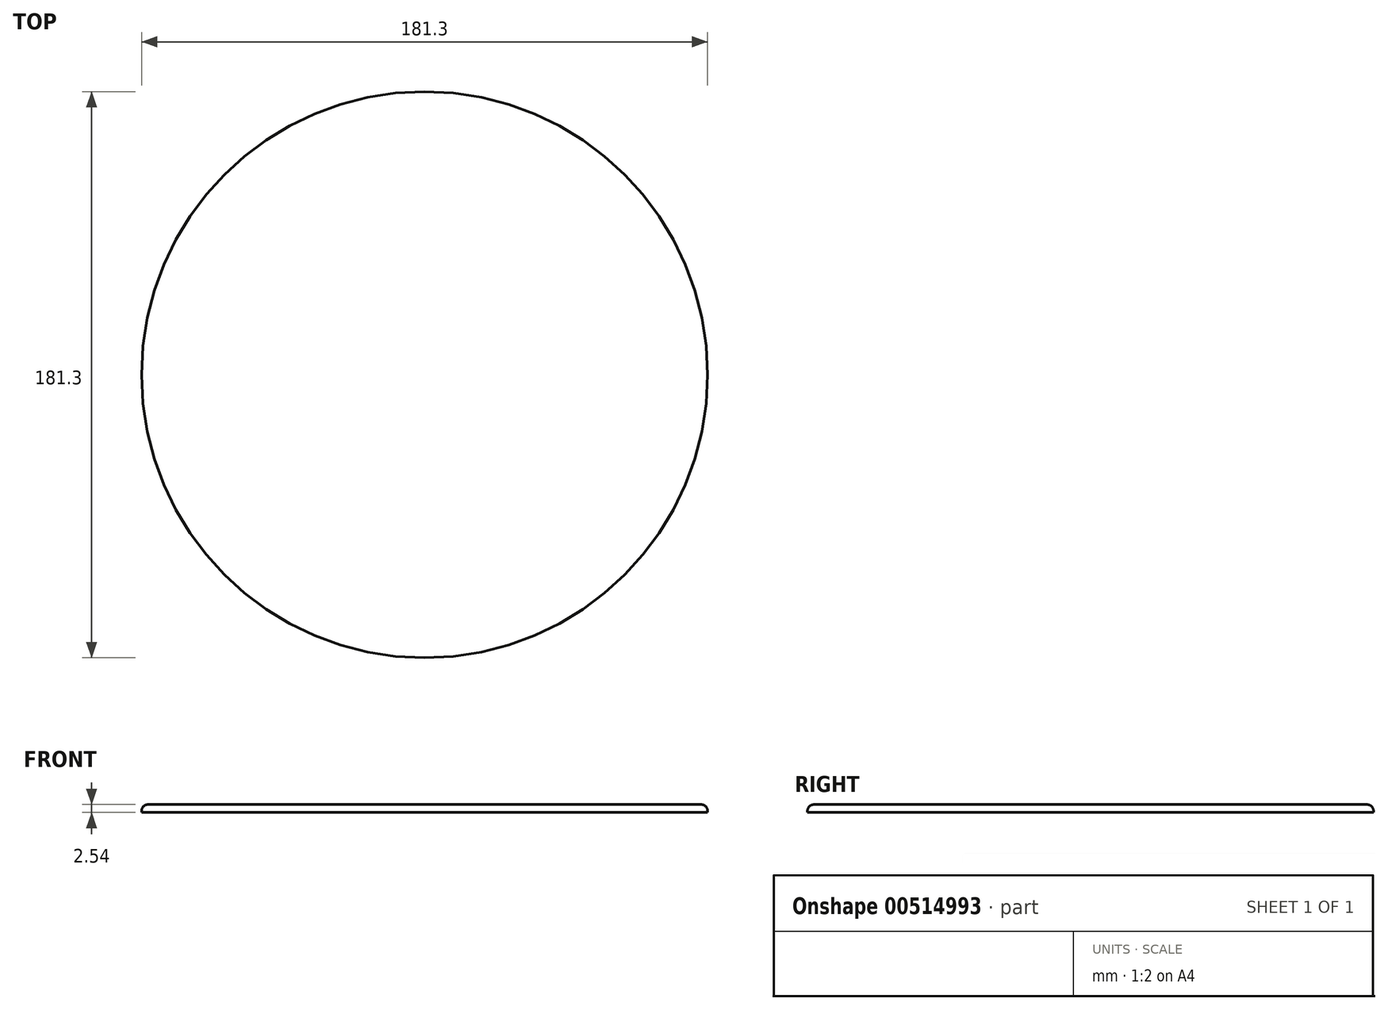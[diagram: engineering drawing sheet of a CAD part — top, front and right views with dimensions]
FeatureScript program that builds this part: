
annotation { "Feature Type Name" : "Feature", "Feature Type Description" : "" }
export const myFeature = defineFeature(function(context is Context, id is Id, definition is map)
    precondition{}
    {
        {
            var Q0;
            Q0=qCreatedBy(makeId("Top.planeOp"),FACE);
            var sketch = newSketch(context, id + "F0", { "sketchPlane" : qUnion([Q0])});
            skCircle(sketch, "E0", {"center": v(0, 0) * mm, "radius": 90.65 * mm});
            skLineSegment(sketch, "E1", {"start": v(0, 0) * mm, "end": v(0, 90.65) * mm});
            skLineSegment(sketch, "E2", {"start": v(0, 0) * mm, "end": v(0, -90.65) * mm});
            skSolve(sketch);
        }
        {
            var Q0;
            Q0 = qSketchRegion(id + "F0", true);
            extrude(context, id + "F1", {"entities" : qUnion([Q0]), "depth" : 2.54 * mm, "offsetDistance" : 25.4 * mm});
        }
        {
            var Q0;
            Q0=makeQuery(id+"F1.opExtrude","CAP_EDGE",EDGE,{"disambiguationData":[OSD([sQuery(id+"F0.wireOp",EDGE,"E0")])],"isStart":false});
            fillet(context, id + "F2", {"entities" : qUnion([Q0]), "radius" : 2 * mm, "tangentPropagation" : true, "allowEdgeOverflow" : false});
        }
    });
